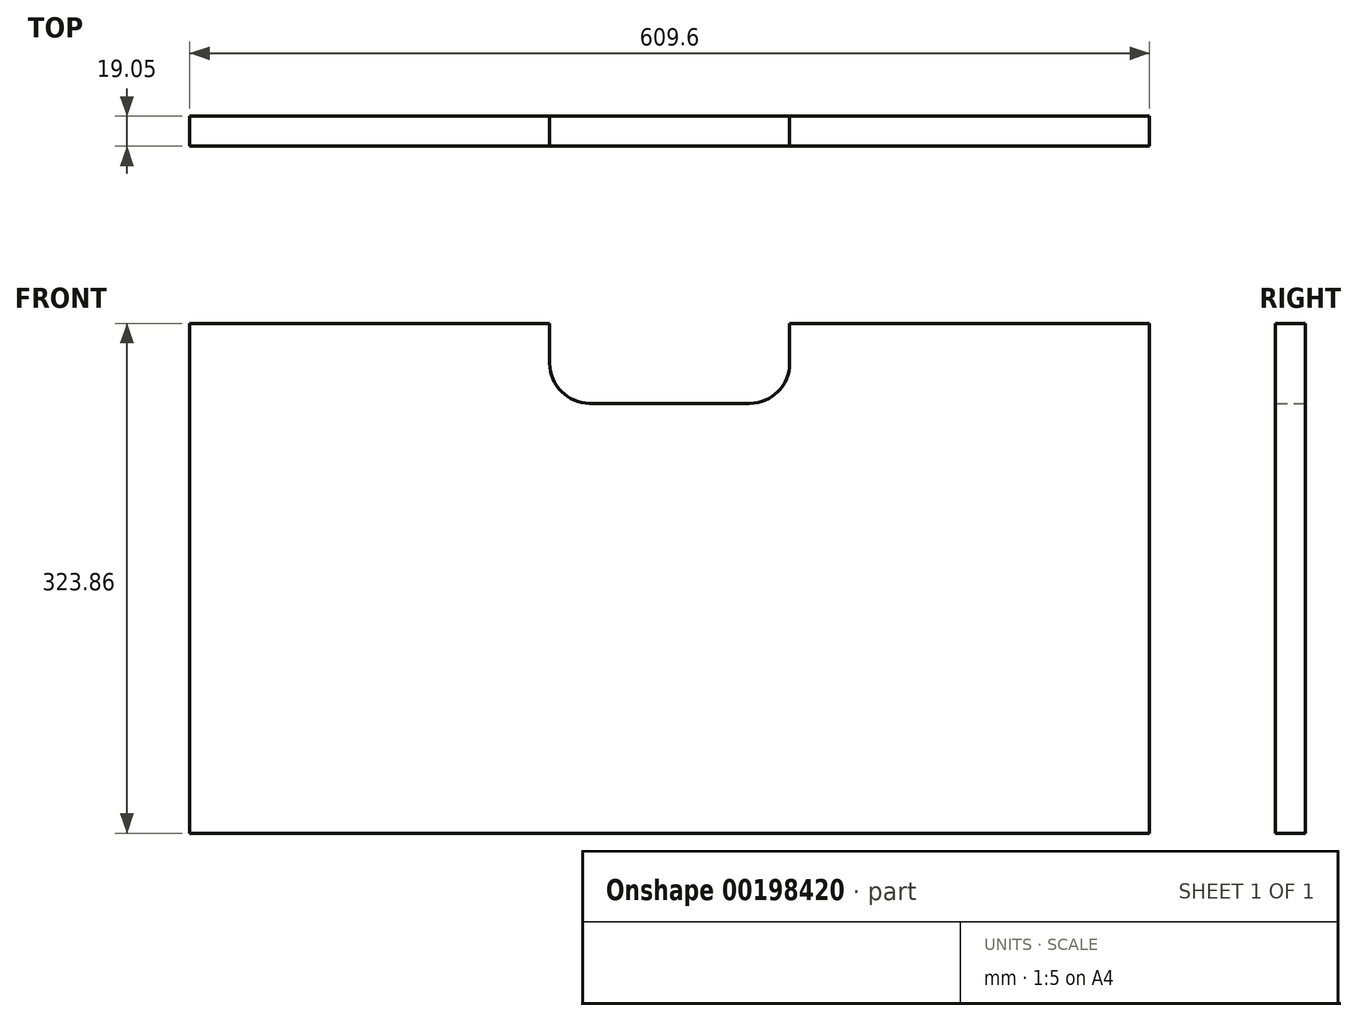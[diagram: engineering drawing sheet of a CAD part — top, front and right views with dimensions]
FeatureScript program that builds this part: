
annotation { "Feature Type Name" : "Feature", "Feature Type Description" : "" }
export const myFeature = defineFeature(function(context is Context, id is Id, definition is map)
    precondition{}
    {
        {
            var Q0;
            Q0=qCreatedBy(makeId("Front.planeOp"),FACE);
            var sketch = newSketch(context, id + "F0", { "sketchPlane" : qUnion([Q0])});
            skLineSegment(sketch, "E0.bottom", {"start": v(-304.8, 161.92) * mm, "end": v(304.8, 161.93) * mm});
            skLineSegment(sketch, "E0.top", {"start": v(-304.8, -161.93) * mm, "end": v(304.8, -161.92) * mm});
            skLineSegment(sketch, "E0.left", {"start": v(-304.8, 161.92) * mm, "end": v(-304.8, -161.93) * mm});
            skLineSegment(sketch, "E0.right", {"start": v(304.8, 161.93) * mm, "end": v(304.8, -161.92) * mm});
            skPoint(sketch, "E0.middle", {"position": v(0, 0) * mm});
            skLineSegment(sketch, "E1.bottom", {"start": v(-76.2, 161.92) * mm, "end": v(76.2, 161.93) * mm});
            skLineSegment(sketch, "E1.top", {"start": v(-50.8, 111.12) * mm, "end": v(50.8, 111.12) * mm});
            skLineSegment(sketch, "E1.left", {"start": v(-76.2, 161.92) * mm, "end": v(-76.2, 136.52) * mm});
            skLineSegment(sketch, "E1.right", {"start": v(76.2, 161.93) * mm, "end": v(76.2, 136.52) * mm});
            skPoint(sketch, "E2.visualSharp", {"position": v(-76.2, 111.12) * mm});
            skArc(sketch, "E2.filletArc", {"start": v(-76.2, 136.52) * mm, "mid": v(-68.76, 118.56) * mm, "end": v(-50.8, 111.12) * mm});
            skPoint(sketch, "E3.visualSharp", {"position": v(76.2, 111.12) * mm});
            skArc(sketch, "E3.filletArc", {"start": v(50.8, 111.12) * mm, "mid": v(68.76, 118.56) * mm, "end": v(76.2, 136.52) * mm});
            skSolve(sketch);
        }
        {
            var Q0;
            Q0=makeQuery(id+"F0.imprint","IMPRINT",FACE,{"disambiguationData":[TD([[makeQuery(id+"F0.imprint","IMPRINT",EDGE,{"derivedFrom":sQuery(id+"F0.wireOp",EDGE,"E0.top")}),1.0]])]});
            extrude(context, id + "F1", {"entities" : qUnion([Q0]), "depth" : 19.05 * mm});
        }
    });
